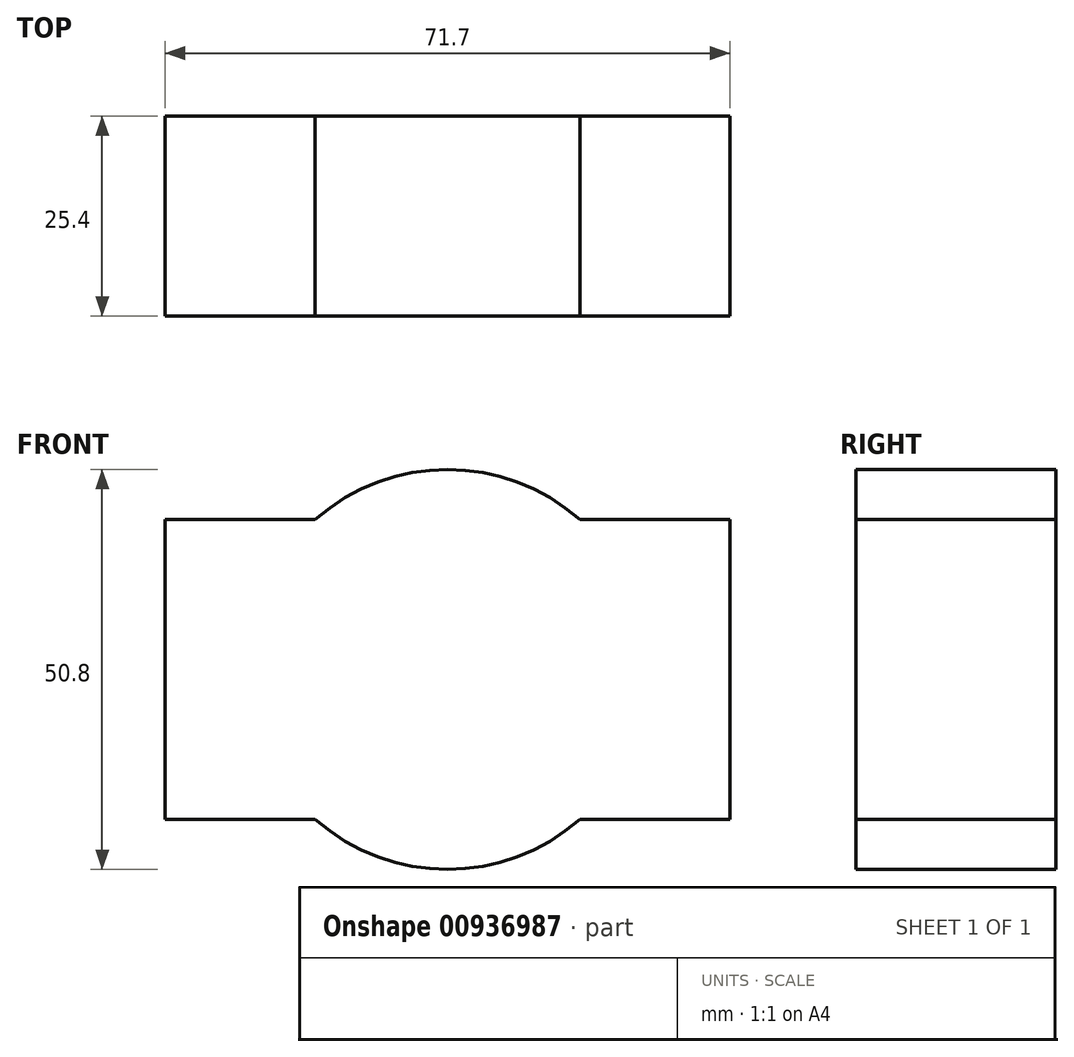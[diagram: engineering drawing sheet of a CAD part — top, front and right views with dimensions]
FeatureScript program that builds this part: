
annotation { "Feature Type Name" : "Feature", "Feature Type Description" : "" }
export const myFeature = defineFeature(function(context is Context, id is Id, definition is map)
    precondition{}
    {
        {
            var Q0;
            Q0=qCreatedBy(makeId("Front.planeOp"),FACE);
            var sketch = newSketch(context, id + "F0", { "sketchPlane" : qUnion([Q0])});
            skLineSegment(sketch, "E0.bottom", {"start": v(35.85, 19.05) * mm, "end": v(16.8, 19.05) * mm});
            skLineSegment(sketch, "E0.top", {"start": v(35.85, -19.05) * mm, "end": v(16.8, -19.05) * mm});
            skLineSegment(sketch, "E0.left", {"start": v(35.85, 19.05) * mm, "end": v(35.85, -19.05) * mm});
            skLineSegment(sketch, "E0.right", {"start": v(-35.85, 19.05) * mm, "end": v(-35.85, -19.05) * mm});
            skPoint(sketch, "E0.middle", {"position": v(0, 0) * mm});
            skArc(sketch, "E1", {"start": v(16.8, 19.05) * mm, "mid": v(0, 25.4) * mm, "end": v(-16.8, 19.05) * mm});
            skLineSegment(sketch, "E2.trimOffspring", {"start": v(-16.8, 19.05) * mm, "end": v(-35.85, 19.05) * mm});
            skLineSegment(sketch, "E3.trimOffspring", {"start": v(-16.8, -19.05) * mm, "end": v(-35.85, -19.05) * mm});
            skArc(sketch, "E4.trimOffspring", {"start": v(-16.8, -19.05) * mm, "mid": v(0, -25.4) * mm, "end": v(16.8, -19.05) * mm});
            skSolve(sketch);
        }
        {
            var Q0;
            Q0=makeQuery(id+"F0.imprint","IMPRINT",FACE,{"disambiguationData":[TD([[makeQuery(id+"F0.imprint","IMPRINT",EDGE,{"derivedFrom":sQuery(id+"F0.wireOp",EDGE,"E0.bottom")}),1.0]])]});
            extrude(context, id + "F1", {"entities" : qUnion([Q0]), "depth" : 25.4 * mm, "offsetDistance" : 25.4 * mm, "symmetric" : true});
        }
    });
